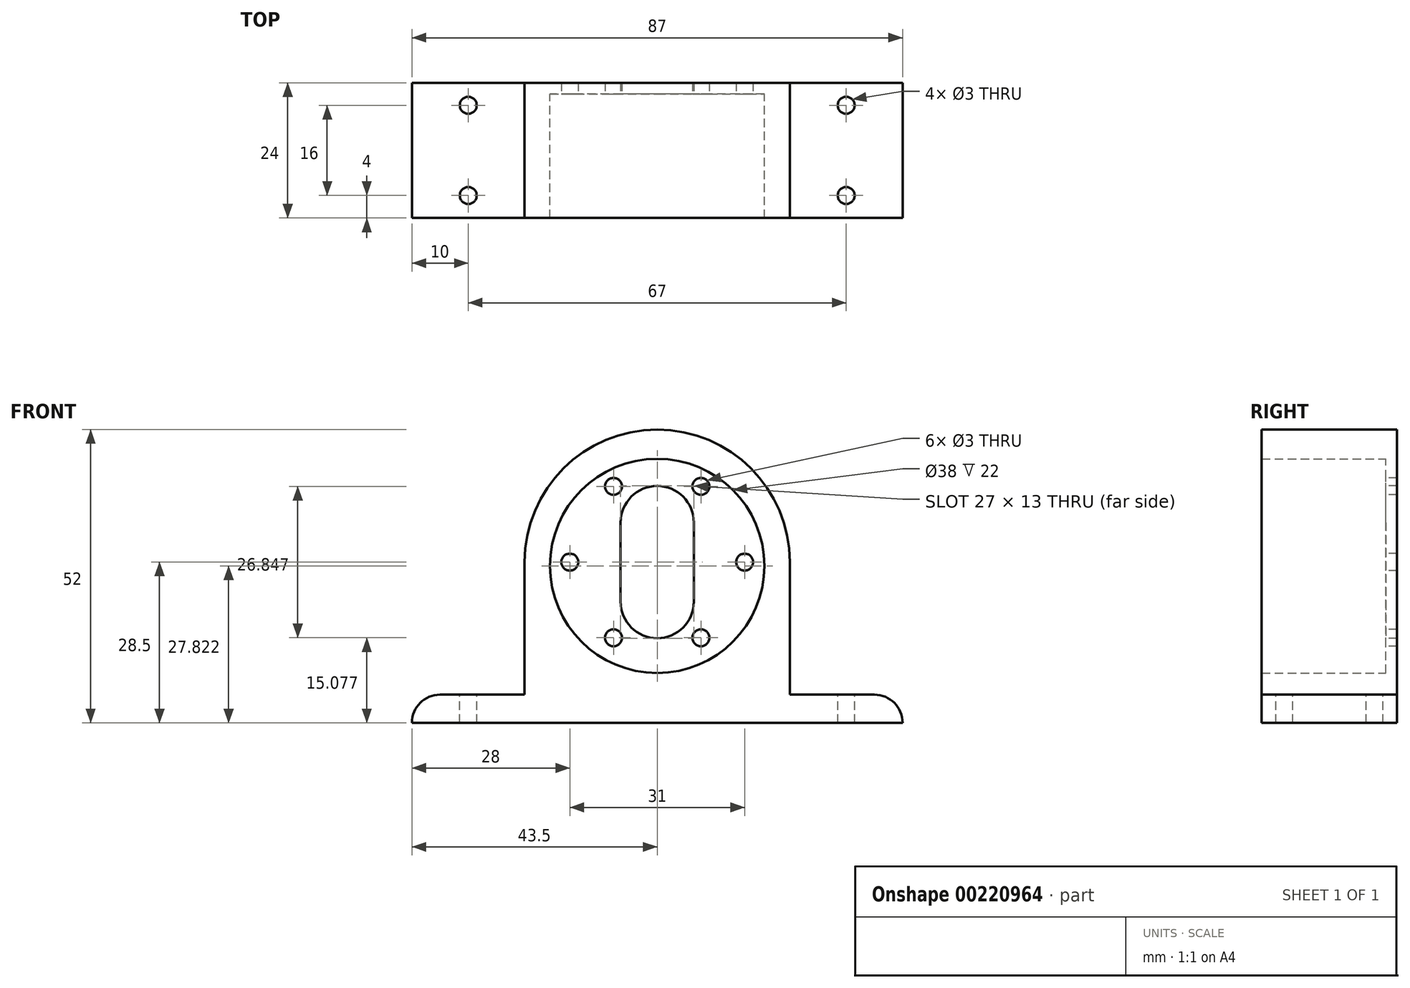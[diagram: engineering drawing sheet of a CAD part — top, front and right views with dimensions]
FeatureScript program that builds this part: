
annotation { "Feature Type Name" : "Feature", "Feature Type Description" : "" }
export const myFeature = defineFeature(function(context is Context, id is Id, definition is map)
    precondition{}
    {
        {
            var Q0;
            Q0=qCreatedBy(makeId("Front.planeOp"),FACE);
            var sketch = newSketch(context, id + "F0", { "sketchPlane" : qUnion([Q0])});
            skLineSegment(sketch, "E0", {"start": v(0, -23.5) * mm, "end": v(-23.5, -23.5) * mm});
            skLineSegment(sketch, "E1", {"start": v(-23.5, -23.5) * mm, "end": v(-23.5, 0) * mm});
            skLineSegment(sketch, "E2", {"start": v(0, -23.5) * mm, "end": v(23.5, -23.5) * mm});
            skLineSegment(sketch, "E3", {"start": v(23.5, -23.5) * mm, "end": v(23.5, 0) * mm});
            skArc(sketch, "E4", {"start": v(-23.5, 0) * mm, "mid": v(0, 23.5) * mm, "end": v(23.5, 0) * mm});
            skSolve(sketch);
        }
        {
            var Q0;
            Q0 = qSketchRegion(id + "F0", true);
            extrude(context, id + "F1", {"entities" : qUnion([Q0]), "depth" : 2 * mm});
        }
        {
            var Q0;
            Q0=makeQuery(id+"F1.opExtrude","CAP_FACE",FACE,{"disambiguationData":[OSD([sQuery(id+"F0.wireOp",EDGE,"E0"),sQuery(id+"F0.wireOp",EDGE,"E1"),sQuery(id+"F0.wireOp",EDGE,"E2"),sQuery(id+"F0.wireOp",EDGE,"E3"),sQuery(id+"F0.wireOp",EDGE,"E4")])],"isStart":false});
            var sketch = newSketch(context, id + "F2", { "sketchPlane" : qUnion([Q0])});
            skCircle(sketch, "E5", {"center": v(15.5, 0) * mm, "radius": 1.5 * mm});
            skCircle(sketch, "E6.1.0", {"center": v(7.75, 13.42) * mm, "radius": 1.5 * mm});
            skCircle(sketch, "E6.2.0", {"center": v(-7.75, 13.42) * mm, "radius": 1.5 * mm});
            skCircle(sketch, "E6.3.0", {"center": v(-15.5, 0) * mm, "radius": 1.5 * mm});
            skCircle(sketch, "E6.4.0", {"center": v(-7.75, -13.42) * mm, "radius": 1.5 * mm});
            skCircle(sketch, "E6.5.0", {"center": v(7.75, -13.42) * mm, "radius": 1.5 * mm});
            skPoint(sketch, "E6.center", {"position": v(0, 0) * mm});
            skLineSegment(sketch, "E7", {"start": v(6.5, 7) * mm, "end": v(6.5, -7) * mm});
            skLineSegment(sketch, "E8", {"start": v(-6.5, -7) * mm, "end": v(-6.5, 7) * mm});
            skArc(sketch, "E9", {"start": v(-6.5, 7) * mm, "mid": v(0, 13.5) * mm, "end": v(6.5, 7) * mm});
            skArc(sketch, "E10", {"start": v(-6.5, -7) * mm, "mid": v(0, -13.5) * mm, "end": v(6.5, -7) * mm});
            skSolve(sketch);
        }
        {
            var Q0;
            Q0 = qSketchRegion(id + "F2", true);
            extrude(context, id + "F3", {"entities" : qUnion([Q0]), "operationType" : NewBodyOperationType.REMOVE, "oppositeDirection" : true, "depth" : 5 * mm});
        }
        {
            var Q0;
            Q0=qCreatedBy(makeId("Front.planeOp"),FACE);
            var sketch = newSketch(context, id + "F4", { "sketchPlane" : qUnion([Q0])});
            skCircle(sketch, "E11", {"center": v(0, -0.68) * mm, "radius": 19 * mm});
            skLineSegment(sketch, "E12", {"start": v(-23.5, 0) * mm, "end": v(-23.5, -23.5) * mm});
            skLineSegment(sketch, "E13", {"start": v(-23.5, -23.5) * mm, "end": v(23.5, -23.5) * mm});
            skLineSegment(sketch, "E14", {"start": v(23.5, -23.5) * mm, "end": v(23.5, 0) * mm});
            skArc(sketch, "E15", {"start": v(-23.5, 0) * mm, "mid": v(0, 23.5) * mm, "end": v(23.5, 0) * mm});
            skSolve(sketch);
        }
        {
            var Q0;
            Q0 = qSketchRegion(id + "F4", true);
            extrude(context, id + "F5", {"entities" : qUnion([Q0]), "operationType" : NewBodyOperationType.ADD, "depth" : 24 * mm});
        }
        {
            var Q0;
            Q0=makeQuery(id+"F5.boolean.opBoolean","MERGE",FACE,{"derivedFrom":[makeQuery(id+"F1.opExtrude","SWEPT_FACE",FACE,{"disambiguationData":[OSD([sQuery(id+"F0.wireOp",EDGE,"E0"),sQuery(id+"F0.wireOp",EDGE,"E2")])]}),makeQuery(id+"F5.opExtrude","SWEPT_FACE",FACE,{"disambiguationData":[OSD([sQuery(id+"F4.wireOp",EDGE,"E13")])]})]});
            var sketch = newSketch(context, id + "F6", { "sketchPlane" : qUnion([Q0])});
            skLineSegment(sketch, "E16.bottom", {"start": v(-23.5, 24) * mm, "end": v(23.5, 24) * mm});
            skLineSegment(sketch, "E16.top", {"start": v(-23.5, 0) * mm, "end": v(23.5, 0) * mm});
            skLineSegment(sketch, "E16.left", {"start": v(-23.5, 24) * mm, "end": v(-23.5, 0) * mm});
            skLineSegment(sketch, "E16.right", {"start": v(23.5, 24) * mm, "end": v(23.5, 0) * mm});
            skSolve(sketch);
        }
        {
            var Q0;
            Q0 = qSketchRegion(id + "F6", true);
            extrude(context, id + "F7", {"entities" : qUnion([Q0]), "operationType" : NewBodyOperationType.ADD, "depth" : 5 * mm});
        }
        {
            var Q0;
            Q0=makeQuery(id+"F7.boolean.opBoolean","MERGE",FACE,{"derivedFrom":[makeQuery(id+"F5.boolean.opBoolean","MERGE",FACE,{"derivedFrom":[makeQuery(id+"F1.opExtrude","SWEPT_FACE",FACE,{"disambiguationData":[OSD([sQuery(id+"F0.wireOp",EDGE,"E1")])]}),makeQuery(id+"F5.opExtrude","SWEPT_FACE",FACE,{"disambiguationData":[OSD([sQuery(id+"F4.wireOp",EDGE,"E12")])]})]}),makeQuery(id+"F7.opExtrude","SWEPT_FACE",FACE,{"disambiguationData":[OSD([sQuery(id+"F6.wireOp",EDGE,"E16.left")])]})]});
            var sketch = newSketch(context, id + "F8", { "sketchPlane" : qUnion([Q0])});
            skLineSegment(sketch, "E17.bottom", {"start": v(0, -28.5) * mm, "end": v(24, -28.5) * mm});
            skLineSegment(sketch, "E17.top", {"start": v(0, -23.5) * mm, "end": v(24, -23.5) * mm});
            skLineSegment(sketch, "E17.left", {"start": v(0, -28.5) * mm, "end": v(0, -23.5) * mm});
            skLineSegment(sketch, "E17.right", {"start": v(24, -28.5) * mm, "end": v(24, -23.5) * mm});
            skSolve(sketch);
        }
        {
            var Q0;
            Q0 = qSketchRegion(id + "F8", true);
            extrude(context, id + "F9", {"entities" : qUnion([Q0]), "operationType" : NewBodyOperationType.ADD, "depth" : 20 * mm});
        }
        {
            var Q0;
            Q0=makeQuery(id+"F9.opExtrude","SWEPT_FACE",FACE,{"disambiguationData":[OSD([sQuery(id+"F8.wireOp",EDGE,"E17.top")])]});
            var sketch = newSketch(context, id + "F10", { "sketchPlane" : qUnion([Q0])});
            skLineSegment(sketch, "E18", {"start": v(-23.5, -12) * mm, "end": v(-33.5, -12) * mm});
            skPoint(sketch, "E18.endSnap0", {"position": v(-23.5, -12) * mm});
            skLineSegment(sketch, "E19", {"start": v(-33.5, -12) * mm, "end": v(-33.5, -4) * mm});
            skLineSegment(sketch, "E20", {"start": v(-33.5, -12) * mm, "end": v(-33.5, -20) * mm});
            skCircle(sketch, "E21", {"center": v(-33.5, -4) * mm, "radius": 1.5 * mm});
            skCircle(sketch, "E22", {"center": v(-33.5, -20) * mm, "radius": 1.5 * mm});
            skSolve(sketch);
        }
        {
            var Q0;
            Q0 = qSketchRegion(id + "F10", true);
            extrude(context, id + "F11", {"entities" : qUnion([Q0]), "operationType" : NewBodyOperationType.REMOVE, "oppositeDirection" : true, "depth" : 25 * mm});
        }
        {
            var Q0;
            Q0=makeQuery(id+"F7.boolean.opBoolean","MERGE",FACE,{"derivedFrom":[makeQuery(id+"F5.boolean.opBoolean","MERGE",FACE,{"derivedFrom":[makeQuery(id+"F1.opExtrude","SWEPT_FACE",FACE,{"disambiguationData":[OSD([sQuery(id+"F0.wireOp",EDGE,"E3")])]}),makeQuery(id+"F5.opExtrude","SWEPT_FACE",FACE,{"disambiguationData":[OSD([sQuery(id+"F4.wireOp",EDGE,"E14")])]})]}),makeQuery(id+"F7.opExtrude","SWEPT_FACE",FACE,{"disambiguationData":[OSD([sQuery(id+"F6.wireOp",EDGE,"E16.right")])]})]});
            var sketch = newSketch(context, id + "F12", { "sketchPlane" : qUnion([Q0])});
            skLineSegment(sketch, "E23.bottom", {"start": v(-24, -28.5) * mm, "end": v(0, -28.5) * mm});
            skLineSegment(sketch, "E23.top", {"start": v(-24, -23.5) * mm, "end": v(0, -23.5) * mm});
            skLineSegment(sketch, "E23.left", {"start": v(-24, -28.5) * mm, "end": v(-24, -23.5) * mm});
            skLineSegment(sketch, "E23.right", {"start": v(0, -28.5) * mm, "end": v(0, -23.5) * mm});
            skSolve(sketch);
        }
        {
            var Q0;
            Q0 = qSketchRegion(id + "F12", true);
            extrude(context, id + "F13", {"entities" : qUnion([Q0]), "operationType" : NewBodyOperationType.ADD, "depth" : 20 * mm});
        }
        {
            var Q0;
            Q0=makeQuery(id+"F13.opExtrude","SWEPT_FACE",FACE,{"disambiguationData":[OSD([sQuery(id+"F12.wireOp",EDGE,"E23.top")])]});
            var sketch = newSketch(context, id + "F14", { "sketchPlane" : qUnion([Q0])});
            skLineSegment(sketch, "E24", {"start": v(23.5, -12) * mm, "end": v(33.5, -12) * mm});
            skLineSegment(sketch, "E25", {"start": v(33.5, -12) * mm, "end": v(33.5, -4) * mm});
            skLineSegment(sketch, "E26", {"start": v(33.5, -12) * mm, "end": v(33.5, -20) * mm});
            skCircle(sketch, "E27", {"center": v(33.5, -20) * mm, "radius": 1.5 * mm});
            skCircle(sketch, "E28", {"center": v(33.5, -4) * mm, "radius": 1.5 * mm});
            skSolve(sketch);
        }
        {
            var Q0;
            Q0 = qSketchRegion(id + "F14", true);
            extrude(context, id + "F15", {"entities" : qUnion([Q0]), "operationType" : NewBodyOperationType.REMOVE, "oppositeDirection" : true, "depth" : 25 * mm});
        }
        {
            var Q0;
            Q0=makeQuery(id+"F13.opExtrude","CAP_EDGE",EDGE,{"disambiguationData":[OSD([sQuery(id+"F12.wireOp",EDGE,"E23.top")])],"isStart":true});
            var Q1;
            Q1=makeQuery(id+"F13.opExtrude","CAP_EDGE",EDGE,{"disambiguationData":[OSD([sQuery(id+"F12.wireOp",EDGE,"E23.top")])],"isStart":false});
            var Q2;
            Q2=makeQuery(id+"F9.opExtrude","CAP_EDGE",EDGE,{"disambiguationData":[OSD([sQuery(id+"F8.wireOp",EDGE,"E17.top")])],"isStart":true});
            var Q3;
            Q3=makeQuery(id+"F9.opExtrude","CAP_EDGE",EDGE,{"disambiguationData":[OSD([sQuery(id+"F8.wireOp",EDGE,"E17.top")])],"isStart":false});
            fillet(context, id + "F16", {"entities" : qUnion([Q0, Q1, Q2, Q3]), "radius" : 5 * mm, "tangentPropagation" : true, "allowEdgeOverflow" : false});
        }
    });
